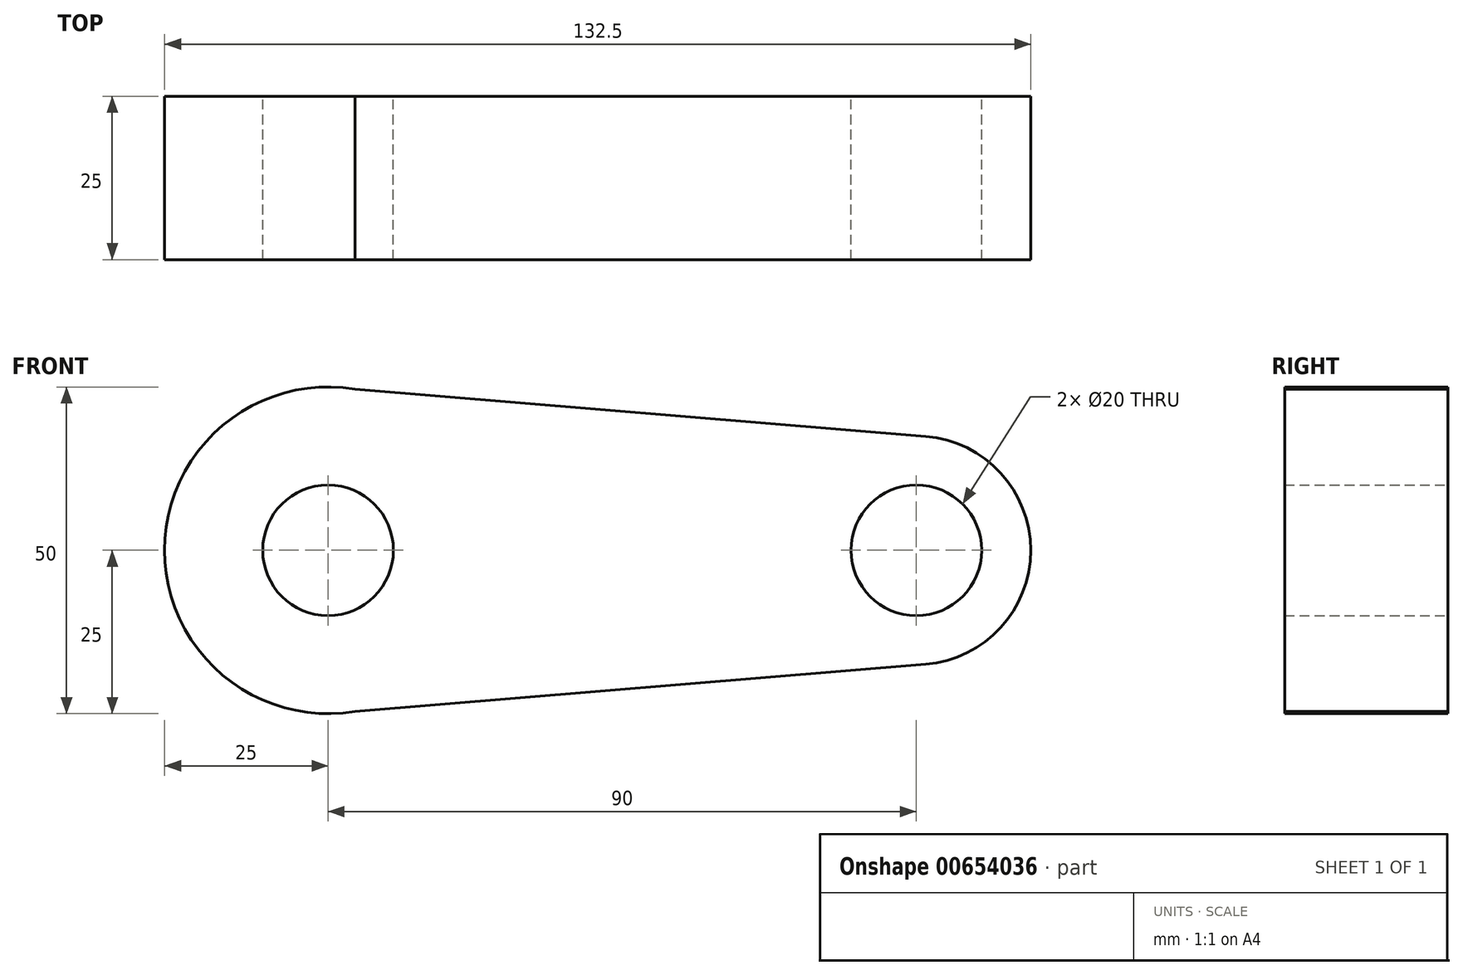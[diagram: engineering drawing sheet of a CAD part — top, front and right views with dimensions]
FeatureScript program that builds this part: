
annotation { "Feature Type Name" : "Feature", "Feature Type Description" : "" }
export const myFeature = defineFeature(function(context is Context, id is Id, definition is map)
    precondition{}
    {
        {
            var Q0;
            Q0=qCreatedBy(makeId("Front.planeOp"),FACE);
            var sketch = newSketch(context, id + "F0", { "sketchPlane" : qUnion([Q0])});
            skCircle(sketch, "E0", {"center": v(90, 0) * mm, "radius": 17.5 * mm});
            skCircle(sketch, "E1", {"center": v(0, 0) * mm, "radius": 25 * mm});
            skLineSegment(sketch, "E2", {"start": v(0, 25) * mm, "end": v(91.44, 17.44) * mm});
            skLineSegment(sketch, "E3", {"start": v(0, -25) * mm, "end": v(91.44, -17.44) * mm});
            skCircle(sketch, "E4", {"center": v(0, 0) * mm, "radius": 10 * mm});
            skCircle(sketch, "E5", {"center": v(90, 0) * mm, "radius": 10 * mm});
            skSolve(sketch);
        }
        {
            var Q0;
            Q0 = qSketchRegion(id + "F0", true);
            extrude(context, id + "F1", {"entities" : qUnion([Q0]), "depth" : 25 * mm, "offsetDistance" : 25 * mm});
        }
    });
